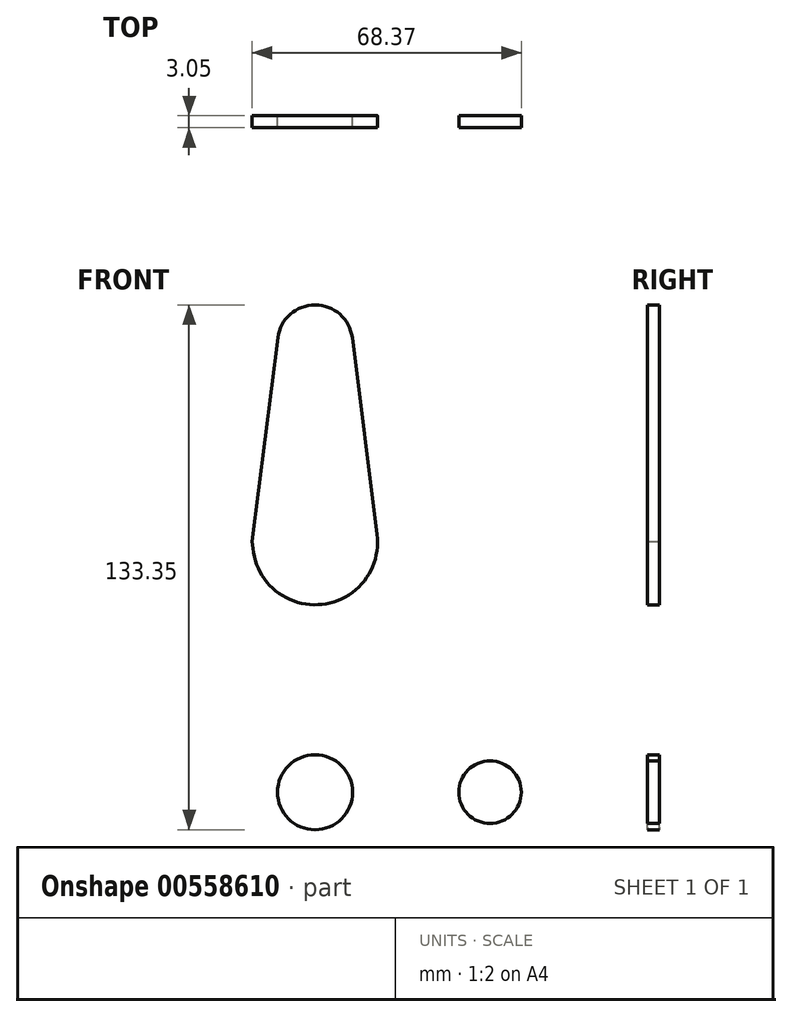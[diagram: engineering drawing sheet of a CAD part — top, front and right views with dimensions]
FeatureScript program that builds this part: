
annotation { "Feature Type Name" : "Feature", "Feature Type Description" : "" }
export const myFeature = defineFeature(function(context is Context, id is Id, definition is map)
    precondition{}
    {
        {
            var Q0;
            Q0=qCreatedBy(makeId("Front.planeOp"),FACE);
            var sketch = newSketch(context, id + "F0", { "sketchPlane" : qUnion([Q0])});
            skLineSegment(sketch, "E0", {"start": v(0, 50.8) * mm, "end": v(0, -63.5) * mm, "construction": true});
            skLineSegment(sketch, "E1", {"start": v(0, -63.5) * mm, "end": v(44.45, -63.5) * mm, "construction": true});
            skCircle(sketch, "E2", {"center": v(0, 50.8) * mm, "radius": 9.53 * mm});
            skCircle(sketch, "E3", {"center": v(0, 0) * mm, "radius": 15.88 * mm});
            skCircle(sketch, "E4", {"center": v(0, -63.5) * mm, "radius": 9.53 * mm});
            skCircle(sketch, "E5", {"center": v(44.45, -63.5) * mm, "radius": 7.94 * mm});
            skLineSegment(sketch, "E6", {"start": v(9.45, 52) * mm, "end": v(16, 0) * mm});
            skLineSegment(sketch, "E7", {"start": v(15.8, -1.59) * mm, "end": v(11.34, -45.91) * mm});
            skLineSegment(sketch, "E8", {"start": v(18.97, -54.65) * mm, "end": v(44.73, -55.57) * mm});
            skLineSegment(sketch, "E9", {"start": v(-9.45, 52) * mm, "end": v(-16, 0) * mm});
            skLineSegment(sketch, "E10", {"start": v(-16, 0.45) * mm, "end": v(-9.57, -63.5) * mm});
            skLineSegment(sketch, "E11", {"start": v(0, -73.03) * mm, "end": v(44.73, -71.43) * mm});
            skCircle(sketch, "E12", {"center": v(0, 50.8) * mm, "radius": 4.4 * mm});
            skCircle(sketch, "E13", {"center": v(-0.14, 36.53) * mm, "radius": 3.04 * mm});
            skCircle(sketch, "E14", {"center": v(0, 0) * mm, "radius": 4.4 * mm});
            skCircle(sketch, "E15", {"center": v(0, -63.5) * mm, "radius": 4.33 * mm});
            skCircle(sketch, "E16", {"center": v(44.45, -63.5) * mm, "radius": 4.33 * mm});
            skPoint(sketch, "E17.newPointA", {"position": v(9.58, -63.5) * mm});
            skArc(sketch, "E17.filletArc", {"start": v(11.34, -45.91) * mm, "mid": v(13.26, -51.93) * mm, "end": v(18.97, -54.65) * mm});
            skSolve(sketch);
        }
        {
            var Q0;
            Q0 = qSketchRegion(id + "F0", true);
            var Q1;
            Q1=makeQuery(id+"F0.imprint","IMPRINT",FACE,{"disambiguationData":[TD([[makeQuery(id+"F0.imprint","IMPRINT",EDGE,{"derivedFrom":sQuery(id+"F0.wireOp",EDGE,"E12")}),1.0]])]});
            var Q2;
            Q2=makeQuery(id+"F0.imprint","IMPRINT",FACE,{"disambiguationData":[TD([[makeQuery(id+"F0.imprint","IMPRINT",EDGE,{"derivedFrom":sQuery(id+"F0.wireOp",EDGE,"E14")}),1.0]])]});
            var Q3;
            Q3=makeQuery(id+"F0.imprint","IMPRINT",FACE,{"disambiguationData":[TD([[makeQuery(id+"F0.imprint","IMPRINT",EDGE,{"derivedFrom":sQuery(id+"F0.wireOp",EDGE,"E15")}),1.0]])]});
            var Q4;
            Q4=makeQuery(id+"F0.imprint","IMPRINT",FACE,{"disambiguationData":[TD([[makeQuery(id+"F0.imprint","IMPRINT",EDGE,{"derivedFrom":sQuery(id+"F0.wireOp",EDGE,"E16")}),1.0]])]});
            var Q5;
            Q5=makeQuery(id+"F0.imprint","IMPRINT",FACE,{"disambiguationData":[TD([[makeQuery(id+"F0.imprint","IMPRINT",EDGE,{"derivedFrom":sQuery(id+"F0.wireOp",EDGE,"E13")}),1.0]])]});
            extrude(context, id + "F1", {"entities" : qUnion([Q0, Q1, Q2, Q3, Q4, Q5]), "depth" : 3.05 * mm, "offsetDistance" : 25.4 * mm});
        }
    });
